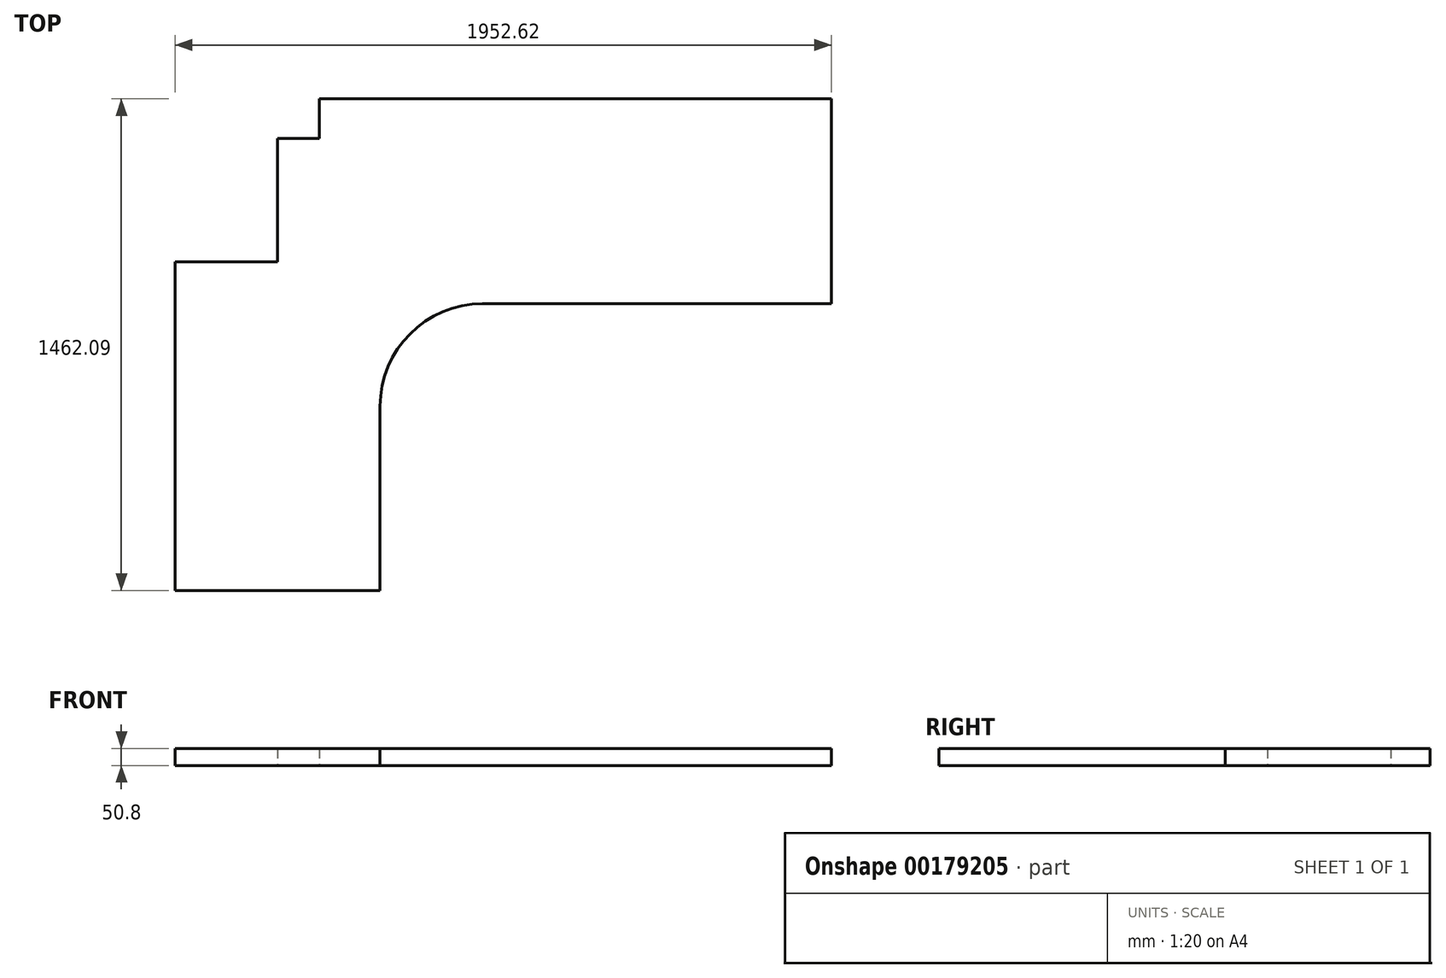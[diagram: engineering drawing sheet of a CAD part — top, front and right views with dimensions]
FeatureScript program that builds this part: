
annotation { "Feature Type Name" : "Feature", "Feature Type Description" : "" }
export const myFeature = defineFeature(function(context is Context, id is Id, definition is map)
    precondition{}
    {
        {
            var Q0;
            Q0=qCreatedBy(makeId("Top.planeOp"),FACE);
            var sketch = newSketch(context, id + "F0", { "sketchPlane" : qUnion([Q0])});
            skLineSegment(sketch, "E0.top", {"start": v(0, -1462.09) * mm, "end": v(609.6, -1462.09) * mm});
            skLineSegment(sketch, "E0.left", {"start": v(0, -484.19) * mm, "end": v(0, -1462.09) * mm});
            skLineSegment(sketch, "E1.bottom", {"start": v(1952.62, -609.6) * mm, "end": v(914.4, -609.6) * mm});
            skLineSegment(sketch, "E1.top", {"start": v(1952.62, 0) * mm, "end": v(428.62, 0) * mm});
            skLineSegment(sketch, "E1.left", {"start": v(1952.62, -609.6) * mm, "end": v(1952.62, 0) * mm});
            skLineSegment(sketch, "E2", {"start": v(0, -484.19) * mm, "end": v(304.8, -484.19) * mm});
            skLineSegment(sketch, "E3", {"start": v(304.8, -484.19) * mm, "end": v(304.8, -117.47) * mm});
            skLineSegment(sketch, "E4", {"start": v(304.8, -117.48) * mm, "end": v(428.62, -117.47) * mm});
            skLineSegment(sketch, "E5", {"start": v(428.62, -117.47) * mm, "end": v(428.62, 0) * mm});
            skLineSegment(sketch, "E6", {"start": v(0, -484.19) * mm, "end": v(0, 0) * mm, "construction": true});
            skLineSegment(sketch, "E7", {"start": v(0, 0) * mm, "end": v(428.62, 0) * mm, "construction": true});
            skLineSegment(sketch, "E8", {"start": v(609.6, -1462.09) * mm, "end": v(609.6, -914.4) * mm});
            skPoint(sketch, "E9.visualSharp", {"position": v(609.6, -609.6) * mm});
            skArc(sketch, "E9.filletArc", {"start": v(914.4, -609.6) * mm, "mid": v(698.87, -698.87) * mm, "end": v(609.6, -914.4) * mm});
            skSolve(sketch);
        }
        {
            var Q0;
            Q0=makeQuery(id+"F0.imprint","IMPRINT",FACE,{"disambiguationData":[TD([[makeQuery(id+"F0.imprint","IMPRINT",EDGE,{"derivedFrom":sQuery(id+"F0.wireOp",EDGE,"E0.top")}),1.0]])]});
            extrude(context, id + "F1", {"entities" : qUnion([Q0]), "depth" : 50.8 * mm});
        }
    });
